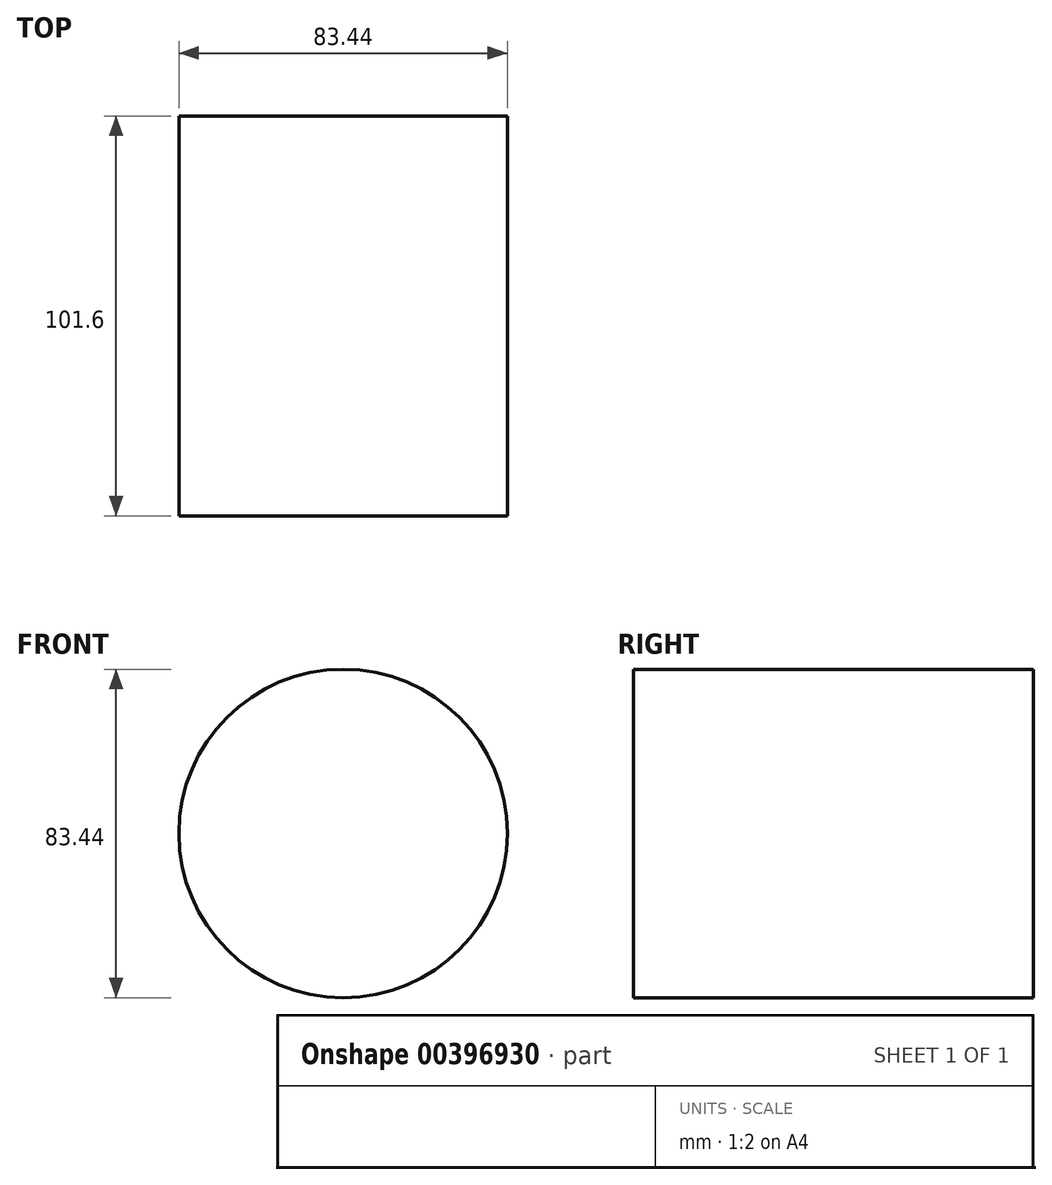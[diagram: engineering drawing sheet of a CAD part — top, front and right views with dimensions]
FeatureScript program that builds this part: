
annotation { "Feature Type Name" : "Feature", "Feature Type Description" : "" }
export const myFeature = defineFeature(function(context is Context, id is Id, definition is map)
    precondition{}
    {
        {
            var Q0;
            Q0=qCreatedBy(makeId("Front.planeOp"),FACE);
            var sketch = newSketch(context, id + "F0", { "sketchPlane" : qUnion([Q0])});
            skCircle(sketch, "E0", {"center": v(0, 0) * mm, "radius": 41.72 * mm});
            skSolve(sketch);
        }
        {
            var Q0;
            Q0 = qSketchRegion(id + "F0", true);
            extrude(context, id + "F1", {"entities" : qUnion([Q0]), "depth" : 101.6 * mm});
        }
        {
            var Q0;
            Q0=makeQuery(id+"F1.opExtrude","CAP_FACE",FACE,{"disambiguationData":[OSD([sQuery(id+"F0.wireOp",EDGE,"E0")])],"isStart":false});
            var sketch = newSketch(context, id + "F2", { "sketchPlane" : qUnion([Q0])});
            skCircle(sketch, "E1", {"center": v(0, 0) * mm, "radius": 38.2 * mm});
            skSolve(sketch);
        }
        {
            var Q0;
            Q0=sQuery(id+"F2.wireOp",EDGE,"E1");
            extrude(context, id + "F3", {"bodyType" : ToolBodyType.SURFACE, "surfaceEntities" : qUnion([Q0]), "oppositeDirection" : true, "depth" : 88.65 * mm});
        }
    });
